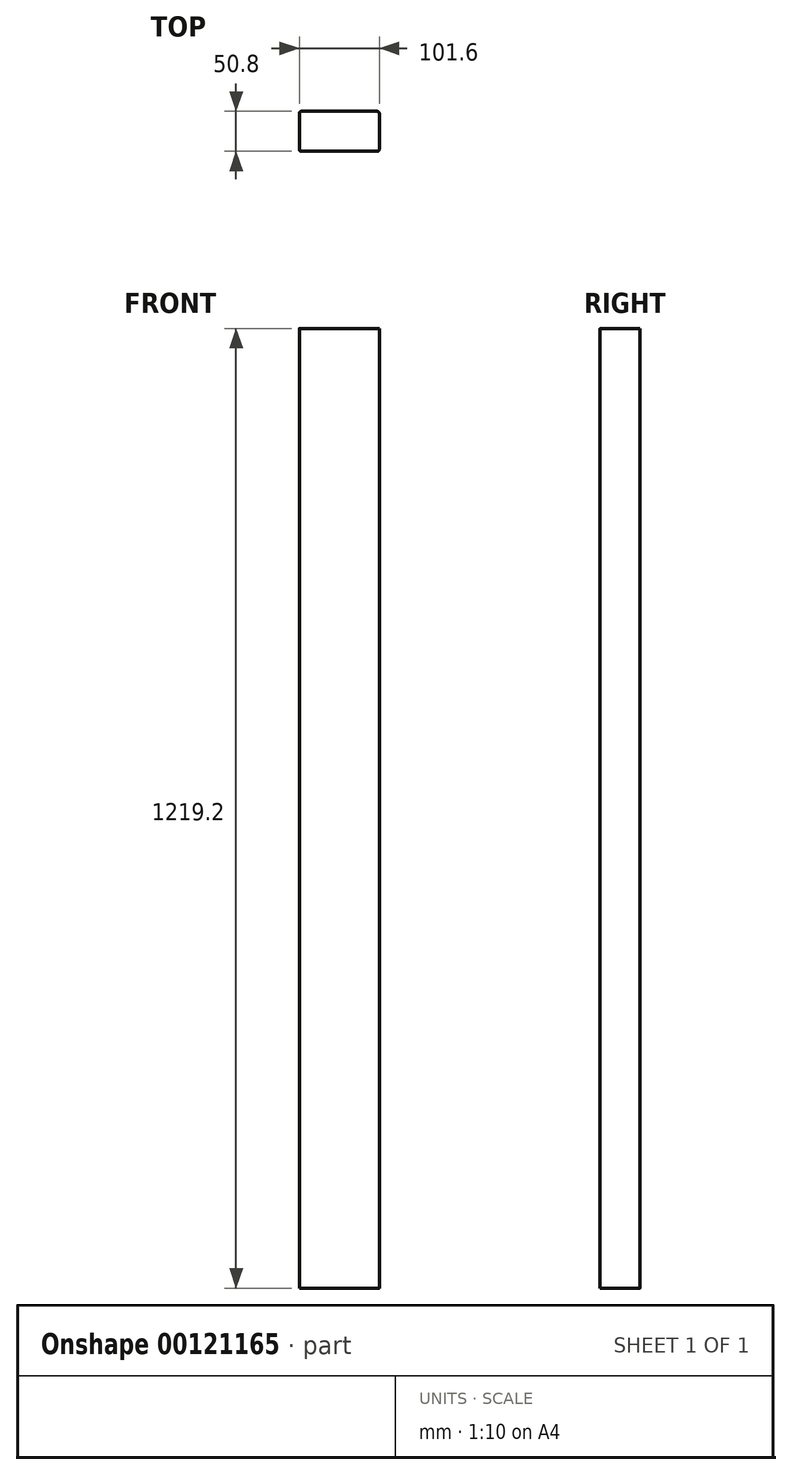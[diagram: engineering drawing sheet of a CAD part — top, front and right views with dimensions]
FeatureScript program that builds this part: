
annotation { "Feature Type Name" : "Feature", "Feature Type Description" : "" }
export const myFeature = defineFeature(function(context is Context, id is Id, definition is map)
    precondition{}
    {
        {
            var Q0;
            Q0=qCreatedBy(makeId("Top.planeOp"),FACE);
            var sketch = newSketch(context, id + "F0", { "sketchPlane" : qUnion([Q0])});
            skLineSegment(sketch, "E0.bottom", {"start": v(2.54, 0) * mm, "end": v(99.06, 0) * mm});
            skLineSegment(sketch, "E0.top", {"start": v(2.54, 50.8) * mm, "end": v(99.06, 50.8) * mm});
            skLineSegment(sketch, "E0.left", {"start": v(0, 2.54) * mm, "end": v(0, 48.26) * mm});
            skLineSegment(sketch, "E0.right", {"start": v(101.6, 2.54) * mm, "end": v(101.6, 48.26) * mm});
            skPoint(sketch, "E1.visualSharp", {"position": v(0, 0) * mm});
            skArc(sketch, "E1.filletArc", {"start": v(0, 2.54) * mm, "mid": v(0.74, 0.74) * mm, "end": v(2.54, 0) * mm});
            skPoint(sketch, "E2.visualSharp", {"position": v(0, 50.8) * mm});
            skArc(sketch, "E2.filletArc", {"start": v(2.54, 50.8) * mm, "mid": v(0.74, 50.06) * mm, "end": v(0, 48.26) * mm});
            skPoint(sketch, "E3.visualSharp", {"position": v(101.6, 50.8) * mm});
            skArc(sketch, "E3.filletArc", {"start": v(101.6, 48.26) * mm, "mid": v(100.86, 50.06) * mm, "end": v(99.06, 50.8) * mm});
            skPoint(sketch, "E4.visualSharp", {"position": v(101.6, 0) * mm});
            skArc(sketch, "E4.filletArc", {"start": v(99.06, 0) * mm, "mid": v(100.86, 0.74) * mm, "end": v(101.6, 2.54) * mm});
            skSolve(sketch);
        }
        {
            var Q0;
            Q0=makeQuery(id+"F0.imprint","IMPRINT",FACE,{"disambiguationData":[TD([[makeQuery(id+"F0.imprint","IMPRINT",EDGE,{"derivedFrom":sQuery(id+"F0.wireOp",EDGE,"E0.bottom")}),1.0]])]});
            extrude(context, id + "F1", {"entities" : qUnion([Q0]), "depth" : 1219.2 * mm});
        }
    });
